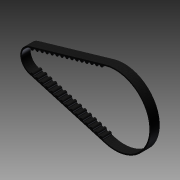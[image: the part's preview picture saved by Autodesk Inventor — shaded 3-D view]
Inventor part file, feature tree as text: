
AUTODESK INVENTOR PART (.ipt)
format: ipt  version: 2012 (Build 160160000, 160)  size: 265,216 bytes
history: native  units: in
note: dims shown in document units (in); Inventor stores cm internally (conversion verified against a paired STEP export)
features: extrude x1, sketch x1
ambient origin geometry x8: Origin, YZ Plane, XZ Plane, XY Plane, X Axis, Y Axis, Z Axis, Center Point
bodies: Solid1 (feature_tree)
feature tree (2):
  extrude  "Extrusion1"  Depth=0.447in
  sketch  "Sketch1"  dims[d0=3.25in d1=0.447in d2=0.5in d4=0.0625in d5=0.024in d7=5.9055in d9=0.204in d10=0.3937in d12=1.0in d14=0.3543in d15=0.0in d16=1.356in d17=0.01in]
